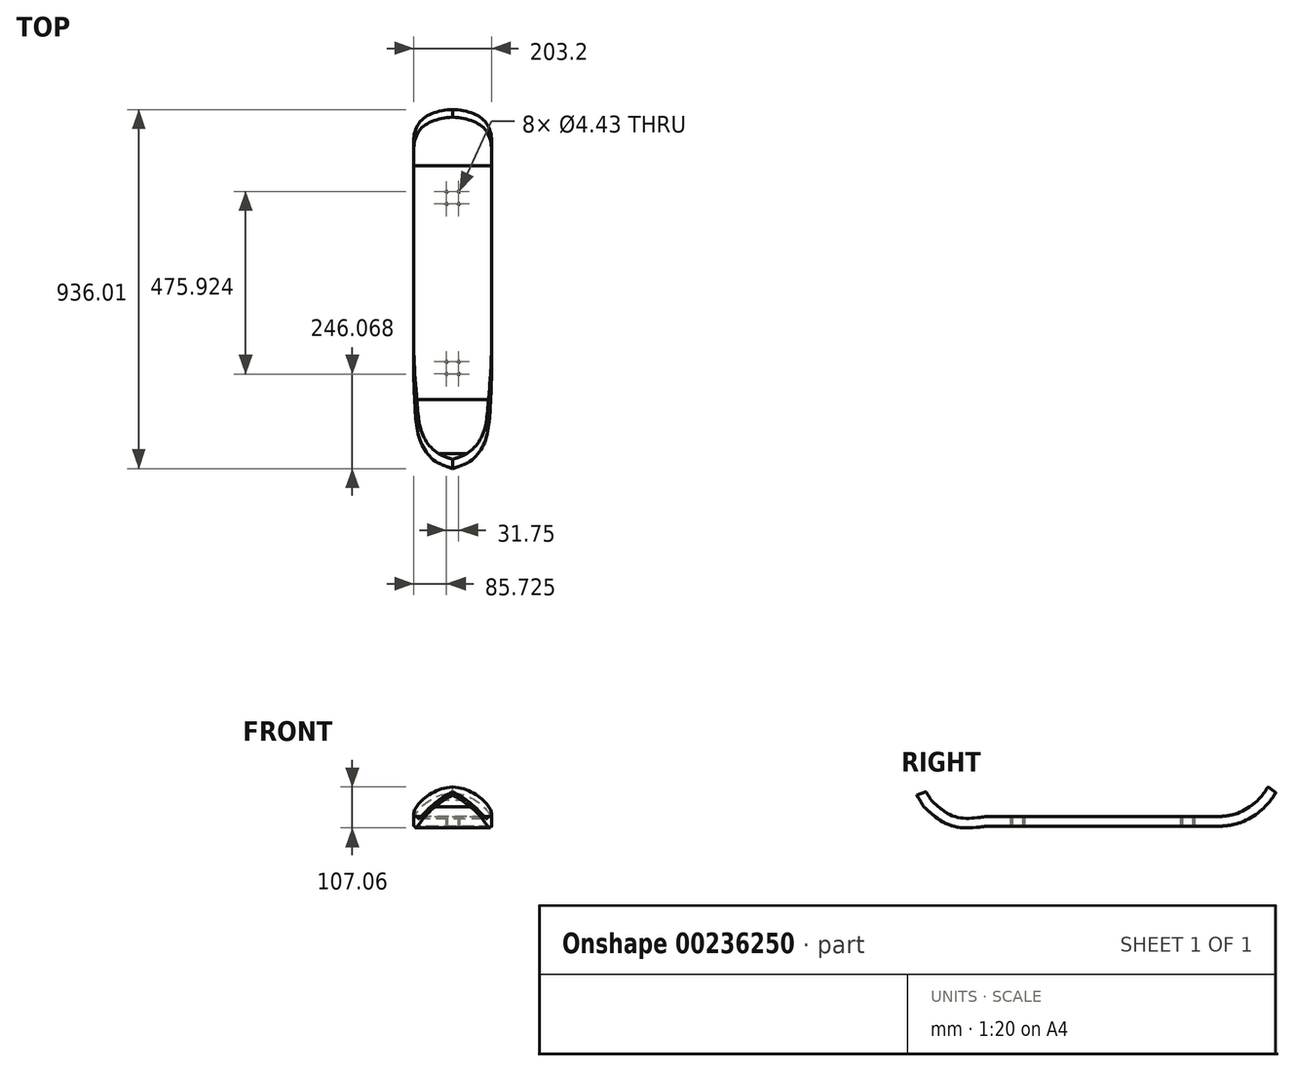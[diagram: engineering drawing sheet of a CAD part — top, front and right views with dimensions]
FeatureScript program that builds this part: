
annotation { "Feature Type Name" : "Feature", "Feature Type Description" : "" }
export const myFeature = defineFeature(function(context is Context, id is Id, definition is map)
    precondition{}
    {
        {
            var Q0;
            Q0=qCreatedBy(makeId("Top.planeOp"),FACE);
            var sketch = newSketch(context, id + "F0", { "sketchPlane" : qUnion([Q0])});
            skLineSegment(sketch, "E0.bottom", {"start": v(101.6, 304.8) * mm, "end": v(-101.6, 304.8) * mm});
            skLineSegment(sketch, "E0.top", {"start": v(101.6, -304.8) * mm, "end": v(-101.6, -304.8) * mm});
            skLineSegment(sketch, "E0.left", {"start": v(101.6, 304.8) * mm, "end": v(101.6, -304.8) * mm});
            skLineSegment(sketch, "E0.right", {"start": v(-101.6, 304.8) * mm, "end": v(-101.6, -304.8) * mm});
            skPoint(sketch, "E0.middle", {"position": v(0, 0) * mm});
            skPoint(sketch, "E1.middle", {"position": v(0, 221.63) * mm});
            skCircle(sketch, "E2", {"center": v(-15.88, 237.5) * mm, "radius": 2.21 * mm});
            skCircle(sketch, "E3", {"center": v(15.87, 237.96) * mm, "radius": 2.21 * mm});
            skCircle(sketch, "E4", {"center": v(15.87, 205.75) * mm, "radius": 2.21 * mm});
            skCircle(sketch, "E5", {"center": v(-15.88, 205.75) * mm, "radius": 2.21 * mm});
            skPoint(sketch, "E1.bottom.end.orphan", {"position": v(-25.4, 247.03) * mm});
            skPoint(sketch, "E1.bottom.start.orphan", {"position": v(25.4, 247.03) * mm});
            skPoint(sketch, "E1.top.end.orphan", {"position": v(-25.4, 196.23) * mm});
            skPoint(sketch, "E1.top.start.orphan", {"position": v(25.4, 196.23) * mm});
            skCircle(sketch, "E6.MirrorC", {"center": v(-15.88, -205.75) * mm, "radius": 2.21 * mm});
            skCircle(sketch, "E7.MirrorC", {"center": v(15.87, -205.75) * mm, "radius": 2.21 * mm});
            skCircle(sketch, "E8.MirrorC", {"center": v(15.87, -237.96) * mm, "radius": 2.21 * mm});
            skCircle(sketch, "E9.MirrorC", {"center": v(-15.88, -237.5) * mm, "radius": 2.21 * mm});
            skSolve(sketch);
        }
        {
            var Q0;
            Q0 = qSketchRegion(id + "F0", true);
            extrude(context, id + "F1", {"entities" : qUnion([Q0]), "endBound" : BoundingType.SYMMETRIC, "depth" : 25.4 * mm});
        }
        {
            var Q0;
            Q0=qCreatedBy(makeId("Right.planeOp"),FACE);
            var sketch = newSketch(context, id + "F2", { "sketchPlane" : qUnion([Q0])});
            skFitSpline(sketch, "E10", {"points": [v(305.82, 0) * mm, v(356.79, 9.48) * mm, v(413.68, 45.64) * mm, v(442.72, 83.57) * mm], "startDerivative": vector(154.7, 13.7) * mm, "endDerivative": vector(79, 123.95) * mm});
            skFitSpline(sketch, "E11", {"points": [v(-304.32, 0) * mm, v(-386.46, 0) * mm, v(-455.83, 46.58) * mm], "startDerivative": vector(-174.45, -25.27) * mm, "endDerivative": vector(-136.16, 130) * mm});
            skFitSpline(sketch, "E12", {"points": [v(-455.83, 46.58) * mm, v(-485.03, 94.04) * mm], "startDerivative": vector(-15.52, 28.3) * mm, "endDerivative": vector(-15.52, 28.3) * mm});
            skSolve(sketch);
        }
        {
            var Q0;
            Q0=makeQuery(id+"F1.opExtrude","SWEPT_FACE",FACE,{"disambiguationData":[OSD([sQuery(id+"F0.wireOp",EDGE,"E0.bottom")])]});
            var Q1;
            Q1=sQuery(id+"F2.wireOp",EDGE,"E10");
            sweep(context, id + "F3", {"operationType" : NewBodyOperationType.ADD, "profiles" : qUnion([Q0]), "path" : qUnion([Q1])});
        }
        {
            var Q0;
            Q0=makeQuery(id+"F1.opExtrude","SWEPT_FACE",FACE,{"disambiguationData":[OSD([sQuery(id+"F0.wireOp",EDGE,"E0.top")])]});
            var Q1;
            Q1=sQuery(id+"F2.wireOp",EDGE,"E11");
            var Q2;
            Q2=sQuery(id+"F2.wireOp",EDGE,"E12");
            sweep(context, id + "F4", {"operationType" : NewBodyOperationType.ADD, "profiles" : qUnion([Q0]), "path" : qUnion([Q1, Q2])});
        }
        {
            var Q0;
            Q0=makeQuery(id+"F4.opSweep","CAP_EDGE",EDGE,{"disambiguationData":[OSD([sQuery(id+"F0.wireOp",EDGE,"E0.top"),sQuery(id+"F0.wireOp",EDGE,"E0.left"),sQuery(id+"F2.wireOp",VERTEX,"E12.end")])],"isStart":false});
            var Q1;
            Q1=makeQuery(id+"F4.opSweep","CAP_EDGE",EDGE,{"disambiguationData":[OSD([sQuery(id+"F0.wireOp",EDGE,"E0.top"),sQuery(id+"F0.wireOp",EDGE,"E0.right"),sQuery(id+"F2.wireOp",VERTEX,"E12.end")])],"isStart":false});
            fillet(context, id + "F5", {"entities" : qUnion([Q0, Q1]), "radius" : 196.23 * mm, "tangentPropagation" : true, "allowEdgeOverflow" : false});
        }
        {
            var Q0;
            Q0=makeQuery(id+"F3.opSweep","CAP_EDGE",EDGE,{"disambiguationData":[OSD([sQuery(id+"F0.wireOp",EDGE,"E0.bottom"),sQuery(id+"F0.wireOp",EDGE,"E0.left"),sQuery(id+"F2.wireOp",VERTEX,"E10.end")])],"isStart":false});
            var Q1;
            Q1=makeQuery(id+"F3.opSweep","CAP_EDGE",EDGE,{"disambiguationData":[OSD([sQuery(id+"F0.wireOp",EDGE,"E0.bottom"),sQuery(id+"F0.wireOp",EDGE,"E0.right"),sQuery(id+"F2.wireOp",VERTEX,"E10.end")])],"isStart":false});
            fillet(context, id + "F6", {"entities" : qUnion([Q0, Q1]), "radius" : 110.38 * mm, "tangentPropagation" : true, "allowEdgeOverflow" : false});
        }
    });
